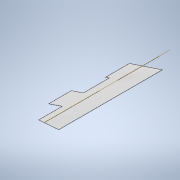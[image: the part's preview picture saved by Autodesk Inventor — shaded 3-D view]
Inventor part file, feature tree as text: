
AUTODESK INVENTOR PART (.ipt)
format: ipt  version: 2022.1 (Build 261234000, 234)  size: 132,608 bytes
history: native  units: in
note: dims shown in document units (in); Inventor stores cm internally (conversion verified against a paired STEP export)
features: sketch x2, extrude x2, plane x1, other x1
ambient origin geometry x8: Origin, YZ Plane, XZ Plane, XY Plane, X Axis, Y Axis, Z Axis, Center Point
bodies: Body1 (feature_tree)
feature tree (6):
  plane  "Work Plane3"
  sketch  "Sketch9"  dims[d38=45.0deg d39=150.0in]
  other  "4-12pictchWorkPlane"
  extrude  "Extrusion8"  Depth=150.0in
  extrude  "Extrusion9"  Depth=1.0in
  sketch  "Sketch10"  dims[d40=157.0in d41=0.1267in d42=86.0in d43=152.0in d44=25.0in d45=164.0in d46=80.0in d47=144.0in d48=90.0in d49=149.0in d50=48.0in d51=1.0in d52=0.0in d53=223.0in d54=238.0in d55=270.0in d56=1.0in d57=0.0in d58=90.0deg]
